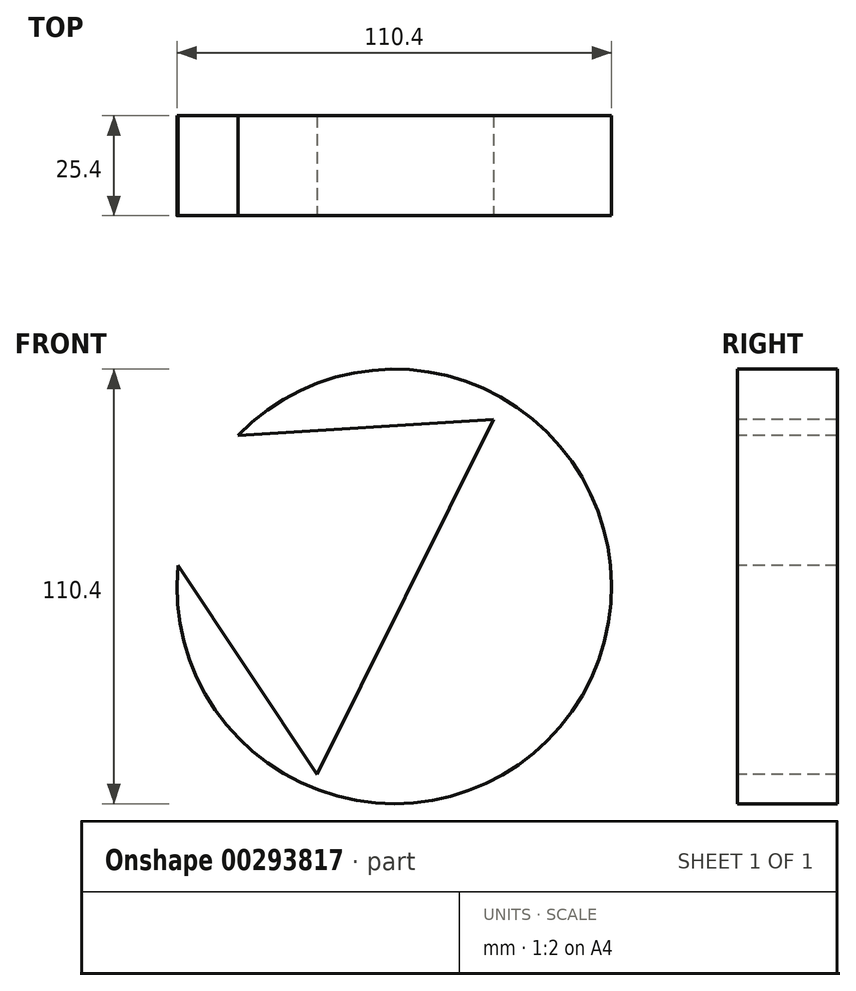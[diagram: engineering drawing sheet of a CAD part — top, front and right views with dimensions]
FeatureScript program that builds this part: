
annotation { "Feature Type Name" : "Feature", "Feature Type Description" : "" }
export const myFeature = defineFeature(function(context is Context, id is Id, definition is map)
    precondition{}
    {
        {
            var Q0;
            Q0=qCreatedBy(makeId("Front.planeOp"),FACE);
            var sketch = newSketch(context, id + "F0", { "sketchPlane" : qUnion([Q0])});
            skCircle(sketch, "E0", {"center": v(-13.85, 10.18) * mm, "radius": 55.2 * mm});
            skCircle(sketch, "E1", {"center": v(14.5, 22.98) * mm, "radius": 127.5 * mm});
            skSolve(sketch);
        }
        {
            var Q0;
            Q0=makeQuery(id+"F0.imprint","IMPRINT",FACE,{"disambiguationData":[TD([[makeQuery(id+"F0.imprint","IMPRINT",EDGE,{"derivedFrom":sQuery(id+"F0.wireOp",EDGE,"E0")}),1.0]])]});
            extrude(context, id + "F1", {"entities" : qUnion([Q0]), "depth" : 25.4 * mm});
        }
        {
            var Q0;
            Q0=makeQuery(id+"F1.opExtrude","CAP_FACE",FACE,{"disambiguationData":[OSD([sQuery(id+"F0.wireOp",EDGE,"E0")])],"isStart":false});
            var sketch = newSketch(context, id + "F2", { "sketchPlane" : qUnion([Q0])});
            skCircle(sketch, "E2.cCircle", {"center": v(-37.1, 20.45) * mm, "radius": 29.08 * mm, "construction": true});
            skLineSegment(sketch, "E2.0", {"start": v(11.33, 52.65) * mm, "end": v(-33.44, -37.6) * mm});
            skLineSegment(sketch, "E2.1", {"start": v(-33.44, -37.6) * mm, "end": v(-89.2, 46.3) * mm});
            skLineSegment(sketch, "E2.2", {"start": v(-89.2, 46.3) * mm, "end": v(11.33, 52.65) * mm});
            skPoint(sketch, "E2.0.midPoint", {"position": v(-11.06, 7.53) * mm});
            skSolve(sketch);
        }
        {
            var Q0;
            {var subQ0=sQuery(id+"F2.wireOp",EDGE,"E2.0");Q0=makeQuery(id+"F2.imprint","IMPRINT",FACE,{"disambiguationData":[TD([[makeQuery(id+"F2.imprint","IMPRINT",EDGE,{"derivedFrom":subQ0}),-1.0]])]});}
            extrude(context, id + "F3", {"entities" : qUnion([Q0]), "operationType" : NewBodyOperationType.REMOVE, "oppositeDirection" : true, "depth" : 25.4 * mm});
        }
    });
